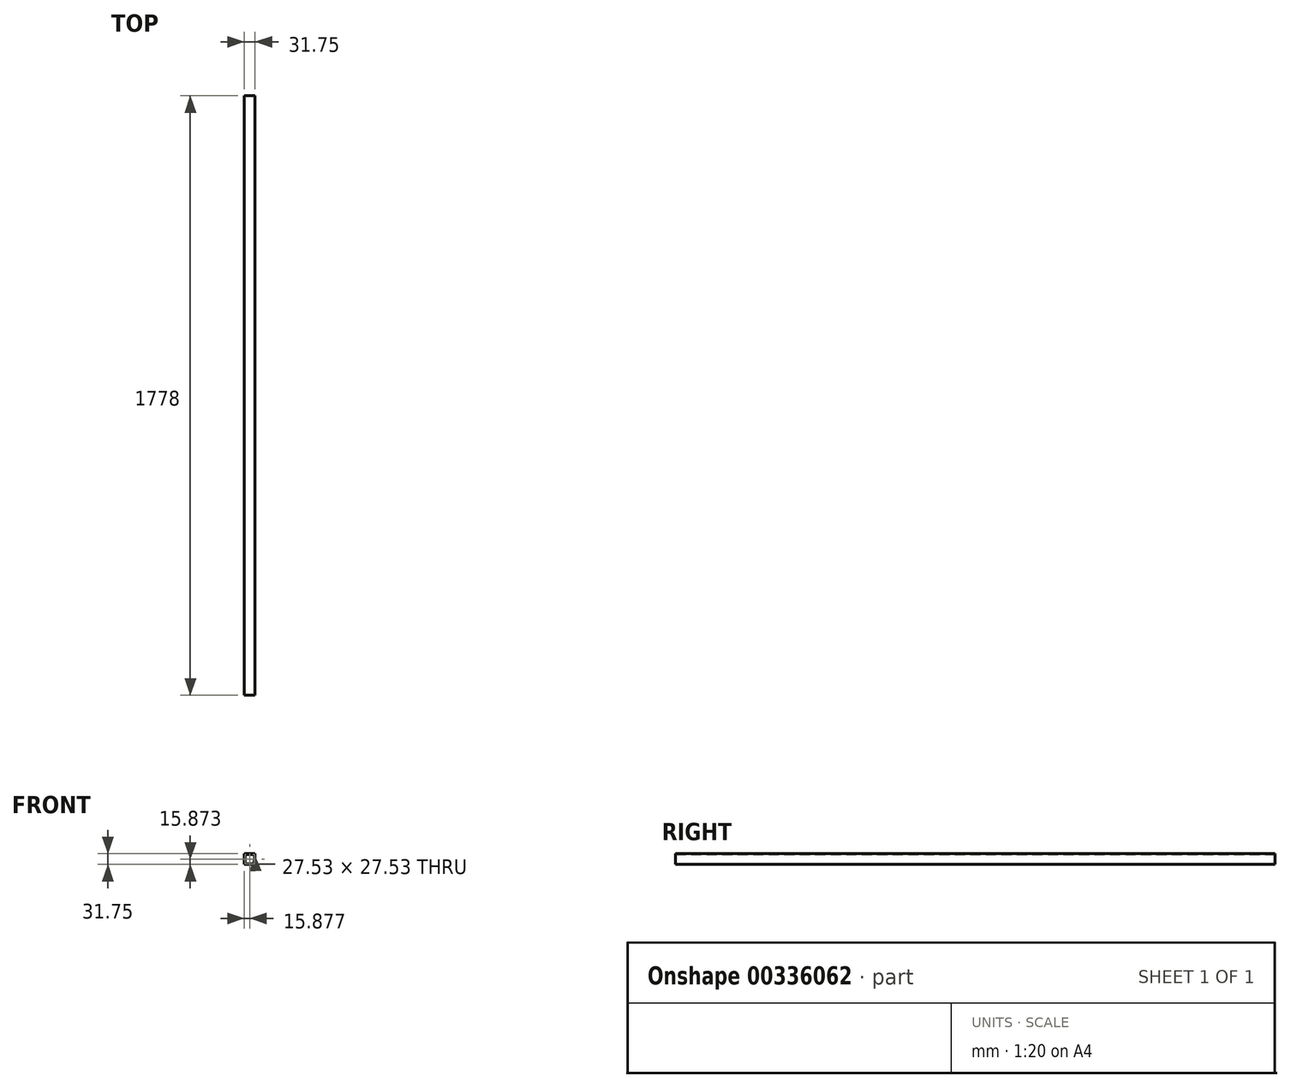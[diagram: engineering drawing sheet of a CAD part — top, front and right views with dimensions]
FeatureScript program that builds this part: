
annotation { "Feature Type Name" : "Feature", "Feature Type Description" : "" }
export const myFeature = defineFeature(function(context is Context, id is Id, definition is map)
    precondition{}
    {
        {
            var Q0;
            Q0=qCreatedBy(makeId("Front.planeOp"),FACE);
            var sketch = newSketch(context, id + "F0", { "sketchPlane" : qUnion([Q0])});
            skLineSegment(sketch, "E0.bottom", {"start": v(-45.93, 18.33) * mm, "end": v(-14.18, 18.33) * mm});
            skLineSegment(sketch, "E0.top", {"start": v(-45.93, -13.42) * mm, "end": v(-14.18, -13.42) * mm});
            skLineSegment(sketch, "E0.left", {"start": v(-45.93, 18.33) * mm, "end": v(-45.93, -13.42) * mm});
            skLineSegment(sketch, "E0.right", {"start": v(-14.18, 18.33) * mm, "end": v(-14.18, -13.42) * mm});
            skLineSegment(sketch, "E1.0", {"start": v(-16.29, 16.22) * mm, "end": v(-16.29, -11.31) * mm});
            skLineSegment(sketch, "E1.1", {"start": v(-43.82, 16.22) * mm, "end": v(-16.29, 16.22) * mm});
            skLineSegment(sketch, "E1.2", {"start": v(-43.82, 16.22) * mm, "end": v(-43.82, -11.31) * mm});
            skLineSegment(sketch, "E1.3", {"start": v(-43.82, -11.31) * mm, "end": v(-16.29, -11.31) * mm});
            skSolve(sketch);
        }
        {
            var Q0;
            Q0 = qSketchRegion(id + "F0", true);
            extrude(context, id + "F1", {"entities" : qUnion([Q0]), "depth" : 1778 * mm});
        }
    });
